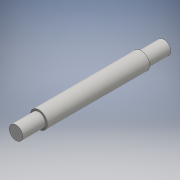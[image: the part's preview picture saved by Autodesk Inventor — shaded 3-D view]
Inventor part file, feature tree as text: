
AUTODESK INVENTOR PART (.ipt)
format: ipt  version: 2016 (Build 200138000, 138)  size: 103,424 bytes
history: native  units: mm
features: extrude x3, sketch x3, other x1
ambient origin geometry x8: Origin, YZ Plane, XZ Plane, XY Plane, X Axis, Y Axis, Z Axis, Center Point
bodies: Body1 (feature_tree)
feature tree (7):
  other  "ソリッド1"
  extrude  "押し出し1"  Depth=15.0mm
  extrude  "押し出し2"  Depth=110.0mm TaperAngle=0.0deg
  extrude  "押し出し3"  Depth=12.0mm
  sketch  "スケッチ1"
  sketch  "スケッチ2"
  sketch  "スケッチ3"
